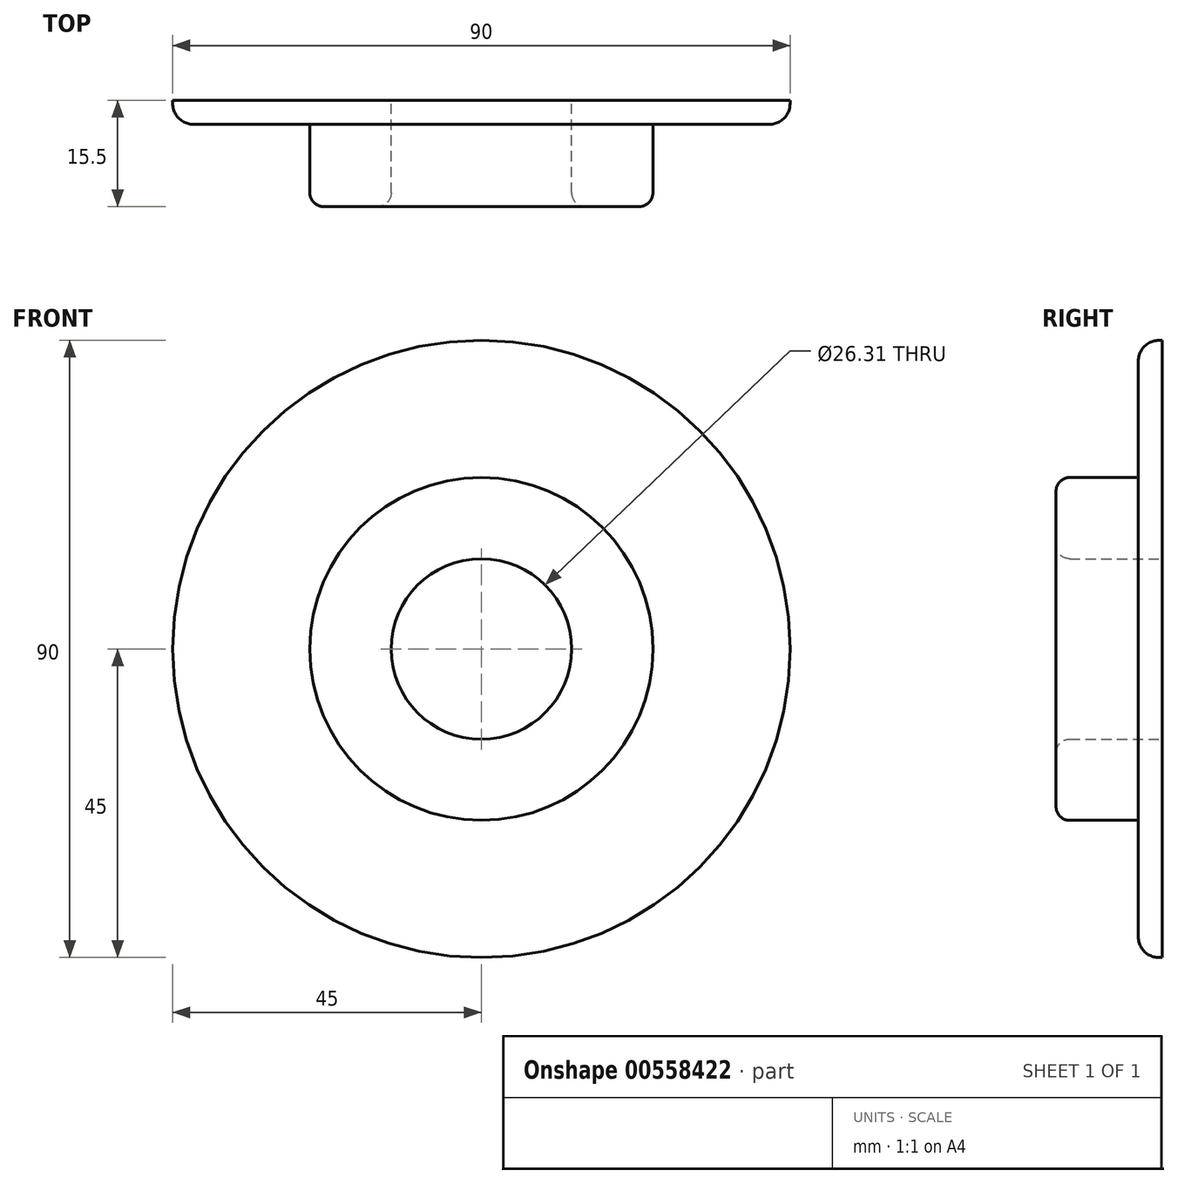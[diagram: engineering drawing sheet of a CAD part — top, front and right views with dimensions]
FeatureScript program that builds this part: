
annotation { "Feature Type Name" : "Feature", "Feature Type Description" : "" }
export const myFeature = defineFeature(function(context is Context, id is Id, definition is map)
    precondition{}
    {
        {
            var Q0;
            Q0=qCreatedBy(makeId("Front.planeOp"),FACE);
            var sketch = newSketch(context, id + "F0", { "sketchPlane" : qUnion([Q0])});
            skCircle(sketch, "E0", {"center": v(0, 0) * mm, "radius": 45 * mm});
            skPoint(sketch, "E0.first.point", {"position": v(-37.72, 24.54) * mm});
            skPoint(sketch, "E0.second.point", {"position": v(-29.14, -34.3) * mm});
            skPoint(sketch, "E0.third.point", {"position": v(33.78, 29.73) * mm});
            skCircle(sketch, "E1", {"center": v(0, 0) * mm, "radius": 13.15 * mm});
            skSolve(sketch);
        }
        {
            var Q0;
            Q0=makeQuery(id+"F0.imprint","IMPRINT",FACE,{"disambiguationData":[TD([[makeQuery(id+"F0.imprint","IMPRINT",EDGE,{"derivedFrom":sQuery(id+"F0.wireOp",EDGE,"E0")}),1.0]])]});
            extrude(context, id + "F1", {"entities" : qUnion([Q0]), "depth" : 3.5 * mm});
        }
        {
            var Q0;
            Q0=makeQuery(id+"F1.opExtrude","CAP_EDGE",EDGE,{"disambiguationData":[OSD([sQuery(id+"F0.wireOp",EDGE,"E0")])],"isStart":false});
            fillet(context, id + "F2", {"entities" : qUnion([Q0]), "radius" : 3 * mm, "tangentPropagation" : true, "allowEdgeOverflow" : false});
        }
        {
            var Q0;
            Q0=makeQuery(id+"F1.opExtrude","CAP_FACE",FACE,{"disambiguationData":[OSD([sQuery(id+"F0.wireOp",EDGE,"E0"),sQuery(id+"F0.wireOp",EDGE,"E1")])],"isStart":false});
            var sketch = newSketch(context, id + "F3", { "sketchPlane" : qUnion([Q0])});
            skCircle(sketch, "E2", {"center": v(0, 0) * mm, "radius": 25 * mm});
            skSolve(sketch);
        }
        {
            var Q0;
            Q0=makeQuery(id+"F3.imprint","IMPRINT",FACE,{"disambiguationData":[TD([[makeQuery(id+"F3.imprint","IMPRINT",EDGE,{"derivedFrom":sQuery(id+"F3.wireOp",EDGE,"E2")}),1.0]])]});
            extrude(context, id + "F4", {"entities" : qUnion([Q0]), "operationType" : NewBodyOperationType.ADD, "depth" : 12 * mm});
        }
        {
            var Q0;
            Q0=makeQuery(id+"F4.opExtrude","CAP_EDGE",EDGE,{"disambiguationData":[OSD([sQuery(id+"F0.wireOp",EDGE,"E1")])],"isStart":false});
            var Q1;
            Q1=makeQuery(id+"F4.opExtrude","CAP_EDGE",EDGE,{"disambiguationData":[OSD([sQuery(id+"F3.wireOp",EDGE,"E2")])],"isStart":false});
            fillet(context, id + "F5", {"entities" : qUnion([Q0, Q1]), "radius" : 2 * mm, "tangentPropagation" : true, "allowEdgeOverflow" : false});
        }
    });
